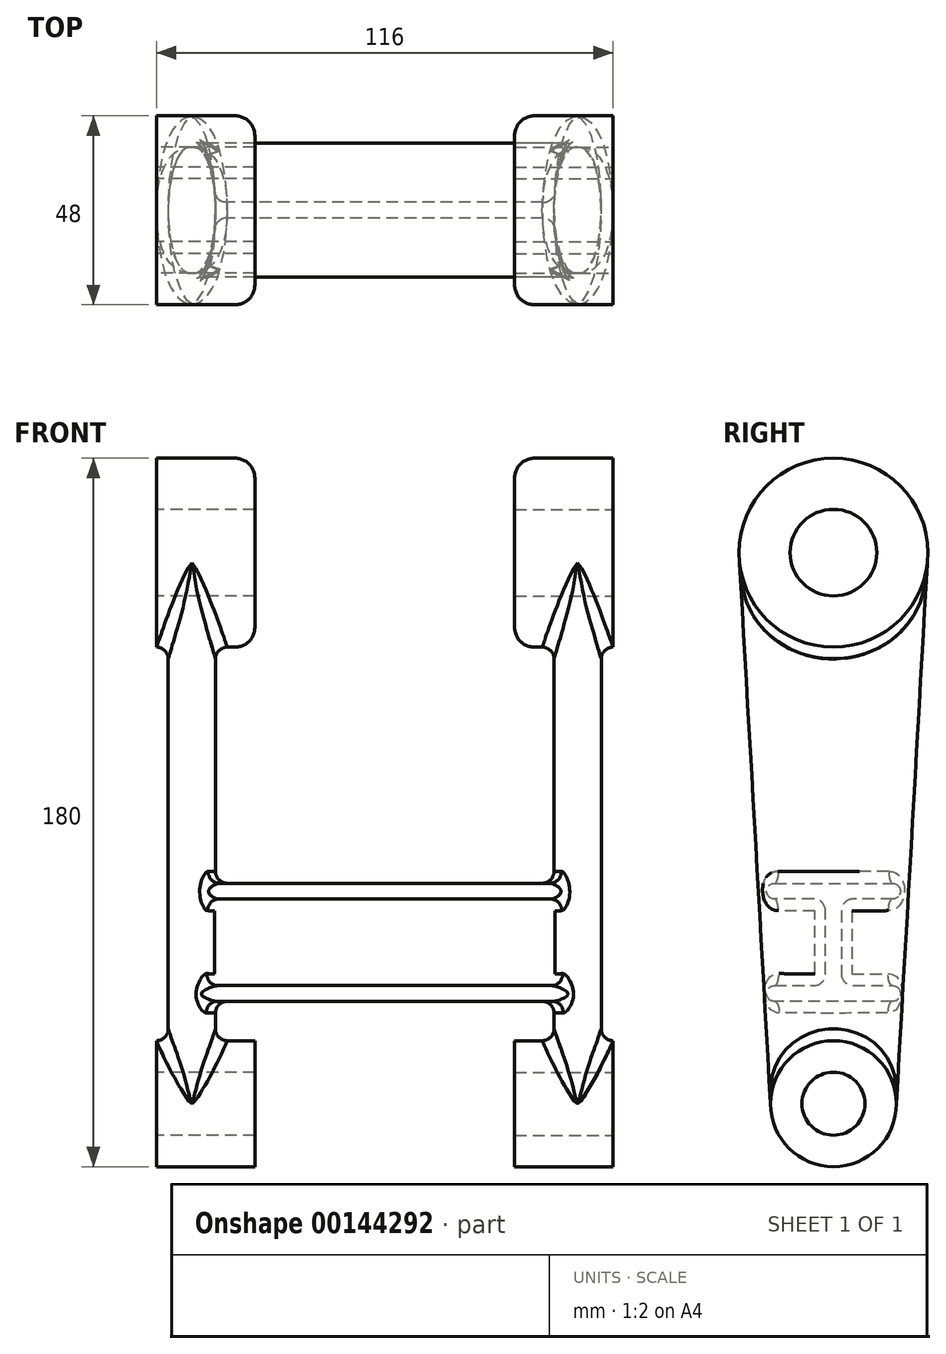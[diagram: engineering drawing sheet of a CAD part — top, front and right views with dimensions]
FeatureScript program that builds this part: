
annotation { "Feature Type Name" : "Feature", "Feature Type Description" : "" }
export const myFeature = defineFeature(function(context is Context, id is Id, definition is map)
    precondition{}
    {
        {
            var Q0;
            Q0=qCreatedBy(makeId("Right.planeOp"),FACE);
            var sketch = newSketch(context, id + "F0", { "sketchPlane" : qUnion([Q0])});
            skCircle(sketch, "E0", {"center": v(0, 0) * mm, "radius": 16 * mm});
            skCircle(sketch, "E1", {"center": v(0, 0) * mm, "radius": 8 * mm});
            skCircle(sketch, "E2", {"center": v(0, 140) * mm, "radius": 24 * mm});
            skCircle(sketch, "E3", {"center": v(0, 140) * mm, "radius": 11 * mm});
            skSolve(sketch);
        }
        {
            var Q0;
            Q0=makeQuery(id+"F0.imprint","IMPRINT",FACE,{"disambiguationData":[TD([[makeQuery(id+"F0.imprint","IMPRINT",EDGE,{"derivedFrom":sQuery(id+"F0.wireOp",EDGE,"E2")}),1.0]])]});
            var Q1;
            Q1=makeQuery(id+"F0.imprint","IMPRINT",FACE,{"disambiguationData":[TD([[makeQuery(id+"F0.imprint","IMPRINT",EDGE,{"derivedFrom":sQuery(id+"F0.wireOp",EDGE,"E3")}),1.0]])]});
            extrude(context, id + "F1", {"entities" : qUnion([Q0, Q1]), "depth" : 25 * mm});
        }
        {
            var Q0;
            Q0=makeQuery(id+"F0.imprint","IMPRINT",FACE,{"disambiguationData":[TD([[makeQuery(id+"F0.imprint","IMPRINT",EDGE,{"derivedFrom":sQuery(id+"F0.wireOp",EDGE,"E0")}),1.0]])]});
            var Q1;
            Q1=makeQuery(id+"F0.imprint","IMPRINT",FACE,{"disambiguationData":[TD([[makeQuery(id+"F0.imprint","IMPRINT",EDGE,{"derivedFrom":sQuery(id+"F0.wireOp",EDGE,"E1")}),1.0]])]});
            extrude(context, id + "F2", {"entities" : qUnion([Q0, Q1]), "depth" : 25 * mm});
        }
        {
            var Q0;
            Q0=qCreatedBy(makeId("Top.planeOp"),FACE);
            var sketch = newSketch(context, id + "F3", { "sketchPlane" : qUnion([Q0])});
            skEllipse(sketch, "E4", {"center": v(9, 0) * mm, "majorRadius": 16 * mm, "minorRadius": 6 * mm, "majorAxis": v(0, -1)});
            skLineSegment(sketch, "E5", {"start": v(0, 16) * mm, "end": v(24.3, 16) * mm, "construction": true});
            skPoint(sketch, "E6", {"position": v(3, 0) * mm});
            skSolve(sketch);
        }
        {
            var Q0;
            Q0=qCreatedBy(makeId("Top.planeOp"),FACE);
            var Q1;
            Q1=sQuery(id+"F0.wireOp",VERTEX,"E3.center");
            cPlane(context, id + "F4", {"entities" : qUnion([Q0, Q1]), "cplaneType" : CPlaneType.PLANE_POINT, "offset" : 25 * mm, "width" : 150 * mm, "height" : 150 * mm});
        }
        {
            var Q0;
            Q0=qCreatedBy(id+"F4.planeOp",FACE);
            var sketch = newSketch(context, id + "F5", { "sketchPlane" : qUnion([Q0])});
            skEllipse(sketch, "E7", {"center": v(9, 0) * mm, "majorRadius": 24 * mm, "minorRadius": 6 * mm, "majorAxis": v(0, -1)});
            skPoint(sketch, "E8", {"position": v(3, 0) * mm});
            skLineSegment(sketch, "E9", {"start": v(0, 24) * mm, "end": v(24.27, 24) * mm, "construction": true});
            skSolve(sketch);
        }
        {
            var Q0;
            Q0 = qSketchRegion(id + "F5", true);
            var Q1;
            Q1 = qSketchRegion(id + "F3", true);
            loft(context, id + "F6", {"operationType" : NewBodyOperationType.ADD, "sheetProfilesArray" : [{ "sheetProfileEntities" : qUnion([Q0]) }, { "sheetProfileEntities" : qUnion([Q1]) }]});
        }
        {
            var Q0;
            Q0=makeQuery(id+"F0.imprint","IMPRINT",FACE,{"disambiguationData":[TD([[makeQuery(id+"F0.imprint","IMPRINT",EDGE,{"derivedFrom":sQuery(id+"F0.wireOp",EDGE,"E3")}),1.0]])]});
            extrude(context, id + "F7", {"entities" : qUnion([Q0]), "operationType" : NewBodyOperationType.REMOVE, "endBound" : BoundingType.THROUGH_ALL, "depth" : 25 * mm});
        }
        {
            var Q0;
            Q0=makeQuery(id+"F0.imprint","IMPRINT",FACE,{"disambiguationData":[TD([[makeQuery(id+"F0.imprint","IMPRINT",EDGE,{"derivedFrom":sQuery(id+"F0.wireOp",EDGE,"E1")}),1.0]])]});
            extrude(context, id + "F8", {"entities" : qUnion([Q0]), "operationType" : NewBodyOperationType.REMOVE, "endBound" : BoundingType.THROUGH_ALL, "depth" : 25 * mm});
        }
        {
            var Q0;
            Q0=qCreatedBy(makeId("Right.planeOp"),FACE);
            cPlane(context, id + "F9", {"entities" : qUnion([Q0]), "cplaneType" : CPlaneType.OFFSET, "offset" : 8 * mm, "width" : 150 * mm, "height" : 150 * mm});
        }
        {
            var Q0;
            Q0=qCreatedBy(id+"F9.planeOp",FACE);
            var sketch = newSketch(context, id + "F10", { "sketchPlane" : qUnion([Q0])});
            skLineSegment(sketch, "E10", {"start": v(-15, 52) * mm, "end": v(-5, 52) * mm});
            skLineSegment(sketch, "E11", {"start": v(-2, 49) * mm, "end": v(-2, 33) * mm});
            skLineSegment(sketch, "E12", {"start": v(-5, 30) * mm, "end": v(-15, 30) * mm});
            skLineSegment(sketch, "E13", {"start": v(-15, 26) * mm, "end": v(15, 26) * mm});
            skLineSegment(sketch, "E14", {"start": v(15, 30) * mm, "end": v(5, 30) * mm});
            skLineSegment(sketch, "E15", {"start": v(2, 33) * mm, "end": v(2, 49) * mm});
            skLineSegment(sketch, "E16", {"start": v(5, 52) * mm, "end": v(15, 52) * mm});
            skLineSegment(sketch, "E17", {"start": v(15, 56) * mm, "end": v(-15, 56) * mm});
            skPoint(sketch, "E18.visualSharp", {"position": v(2, 52) * mm});
            skArc(sketch, "E18.filletArc", {"start": v(5, 52) * mm, "mid": v(2.88, 51.12) * mm, "end": v(2, 49) * mm});
            skPoint(sketch, "E19.visualSharp", {"position": v(-2, 52) * mm});
            skArc(sketch, "E19.filletArc", {"start": v(-2, 49) * mm, "mid": v(-2.88, 51.12) * mm, "end": v(-5, 52) * mm});
            skPoint(sketch, "E20.visualSharp", {"position": v(-2, 30) * mm});
            skArc(sketch, "E20.filletArc", {"start": v(-5, 30) * mm, "mid": v(-2.88, 30.88) * mm, "end": v(-2, 33) * mm});
            skPoint(sketch, "E21.visualSharp", {"position": v(2, 30) * mm});
            skArc(sketch, "E21.filletArc", {"start": v(2, 33) * mm, "mid": v(2.88, 30.88) * mm, "end": v(5, 30) * mm});
            skArc(sketch, "E22", {"start": v(15, 52) * mm, "mid": v(17, 54) * mm, "end": v(15, 56) * mm});
            skArc(sketch, "E23", {"start": v(-15, 56) * mm, "mid": v(-17, 54) * mm, "end": v(-15, 52) * mm});
            skArc(sketch, "E24", {"start": v(-15, 30) * mm, "mid": v(-17, 28) * mm, "end": v(-15, 26) * mm});
            skArc(sketch, "E25", {"start": v(15, 26) * mm, "mid": v(17, 28) * mm, "end": v(15, 30) * mm});
            skPoint(sketch, "E26", {"position": v(0, 56) * mm});
            skPoint(sketch, "E27", {"position": v(0, 26) * mm});
            skLineSegment(sketch, "E28", {"start": v(16, 0) * mm, "end": v(24, 140) * mm, "construction": true});
            skSolve(sketch);
        }
        {
            var Q0;
            Q0 = qSketchRegion(id + "F10", true);
            extrude(context, id + "F11", {"entities" : qUnion([Q0]), "operationType" : NewBodyOperationType.ADD, "depth" : 52 * mm});
        }
        {
            var Q0;
            Q0=qCreatedBy(makeId("Right.planeOp"),FACE);
            cPlane(context, id + "F12", {"entities" : qUnion([Q0]), "cplaneType" : CPlaneType.OFFSET, "offset" : 58 * mm, "width" : 150 * mm, "height" : 150 * mm});
        }
        {
            var Q0;
            Q0=makeQuery(id+"F1.opExtrude","SWEPT_BODY",BODY,{"disambiguationData":[OSD([sQuery(id+"F0.wireOp",EDGE,"E2")])]});
            var Q1;
            Q1=qCreatedBy(id+"F12.planeOp",FACE);
            mirror(context, id + "F13", {"operationType" : NewBodyOperationType.ADD, "entities" : qUnion([Q0]), "mirrorPlane" : qUnion([Q1])});
        }
        {
            var Q0;
            Q0=makeQuery(id+"F11.boolean.opBoolean","INTERSECT",EDGE,{"derivedFrom":[makeQuery(id+"F6.opLoft","SWEPT_FACE",FACE,{"disambiguationData":[OSD([sQuery(id+"F3.wireOp",EDGE,"E4"),sQuery(id+"F5.wireOp",EDGE,"E7")])]}),makeQuery(id+"F11.opExtrude","SWEPT_FACE",FACE,{"disambiguationData":[OSD([sQuery(id+"F10.wireOp",EDGE,"E17")])]})]});
            var Q1;
            Q1=makeQuery(id+"F11.boolean.opBoolean","INTERSECT",EDGE,{"derivedFrom":[makeQuery(id+"F6.opLoft","SWEPT_FACE",FACE,{"disambiguationData":[OSD([sQuery(id+"F3.wireOp",EDGE,"E4"),sQuery(id+"F5.wireOp",EDGE,"E7")])]}),makeQuery(id+"F11.opExtrude","SWEPT_FACE",FACE,{"disambiguationData":[OSD([sQuery(id+"F10.wireOp",EDGE,"E23")])]})]});
            var Q2;
            Q2=makeQuery(id+"F6.boolean.opBoolean","INTERSECT",EDGE,{"derivedFrom":[makeQuery(id+"F2.opExtrude","SWEPT_FACE",FACE,{"disambiguationData":[OSD([sQuery(id+"F0.wireOp",EDGE,"E0")])]}),makeQuery(id+"F6.opLoft","SWEPT_FACE",FACE,{"disambiguationData":[OSD([sQuery(id+"F3.wireOp",EDGE,"E4"),sQuery(id+"F5.wireOp",EDGE,"E7")])]})]});
            var Q3;
            Q3=makeQuery(id+"F6.boolean.opBoolean","INTERSECT",EDGE,{"derivedFrom":[makeQuery(id+"F1.opExtrude","SWEPT_FACE",FACE,{"disambiguationData":[OSD([sQuery(id+"F0.wireOp",EDGE,"E2")])]}),makeQuery(id+"F6.opLoft","SWEPT_FACE",FACE,{"disambiguationData":[OSD([sQuery(id+"F3.wireOp",EDGE,"E4"),sQuery(id+"F5.wireOp",EDGE,"E7")])]})]});
            var Q4;
            Q4=makeQuery(id+"F6.opLoft","SWEPT_FACE",FACE,{"disambiguationData":[OSD([sQuery(id+"F3.wireOp",EDGE,"E4"),sQuery(id+"F5.wireOp",EDGE,"E7")])]});
            var Q5;
            Q5=makeQuery(id+"F13.opPattern","COPY",EDGE,{"derivedFrom":makeQuery(id+"F6.boolean.opBoolean","INTERSECT",EDGE,{"derivedFrom":[makeQuery(id+"F1.opExtrude","SWEPT_FACE",FACE,{"disambiguationData":[OSD([sQuery(id+"F0.wireOp",EDGE,"E2")])]}),makeQuery(id+"F6.opLoft","SWEPT_FACE",FACE,{"disambiguationData":[OSD([sQuery(id+"F3.wireOp",EDGE,"E4"),sQuery(id+"F5.wireOp",EDGE,"E7")])]})]}),"instanceName":"1"});
            var Q6;
            Q6=makeQuery(id+"F13.opPattern","COPY",EDGE,{"derivedFrom":makeQuery(id+"F6.boolean.opBoolean","INTERSECT",EDGE,{"derivedFrom":[makeQuery(id+"F2.opExtrude","SWEPT_FACE",FACE,{"disambiguationData":[OSD([sQuery(id+"F0.wireOp",EDGE,"E0")])]}),makeQuery(id+"F6.opLoft","SWEPT_FACE",FACE,{"disambiguationData":[OSD([sQuery(id+"F3.wireOp",EDGE,"E4"),sQuery(id+"F5.wireOp",EDGE,"E7")])]})]}),"instanceName":"1"});
            var Q7;
            Q7=makeQuery(id+"F13.opPattern","COPY",EDGE,{"derivedFrom":makeQuery(id+"F11.boolean.opBoolean","INTERSECT",EDGE,{"derivedFrom":[makeQuery(id+"F6.opLoft","SWEPT_FACE",FACE,{"disambiguationData":[OSD([sQuery(id+"F3.wireOp",EDGE,"E4"),sQuery(id+"F5.wireOp",EDGE,"E7")])]}),makeQuery(id+"F11.opExtrude","SWEPT_FACE",FACE,{"disambiguationData":[OSD([sQuery(id+"F10.wireOp",EDGE,"E11")])]})]}),"instanceName":"1"});
            fillet(context, id + "F14", {"entities" : qUnion([Q0, Q1, Q2, Q3, Q4, Q5, Q6, Q7]), "radius" : 3 * mm, "tangentPropagation" : true, "allowEdgeOverflow" : false});
        }
        {
            var Q0;
            Q0=makeQuery(id+"F13.opPattern","COPY",EDGE,{"derivedFrom":makeQuery(id+"F1.opExtrude","CAP_EDGE",EDGE,{"disambiguationData":[OSD([sQuery(id+"F0.wireOp",EDGE,"E2")])],"isStart":false}),"instanceName":"1"});
            var Q1;
            Q1=makeQuery(id+"F1.opExtrude","CAP_EDGE",EDGE,{"disambiguationData":[OSD([sQuery(id+"F0.wireOp",EDGE,"E2")])],"isStart":false});
            fillet(context, id + "F15", {"entities" : qUnion([Q0, Q1]), "radius" : 5 * mm, "tangentPropagation" : true, "allowEdgeOverflow" : false});
        }
    });
